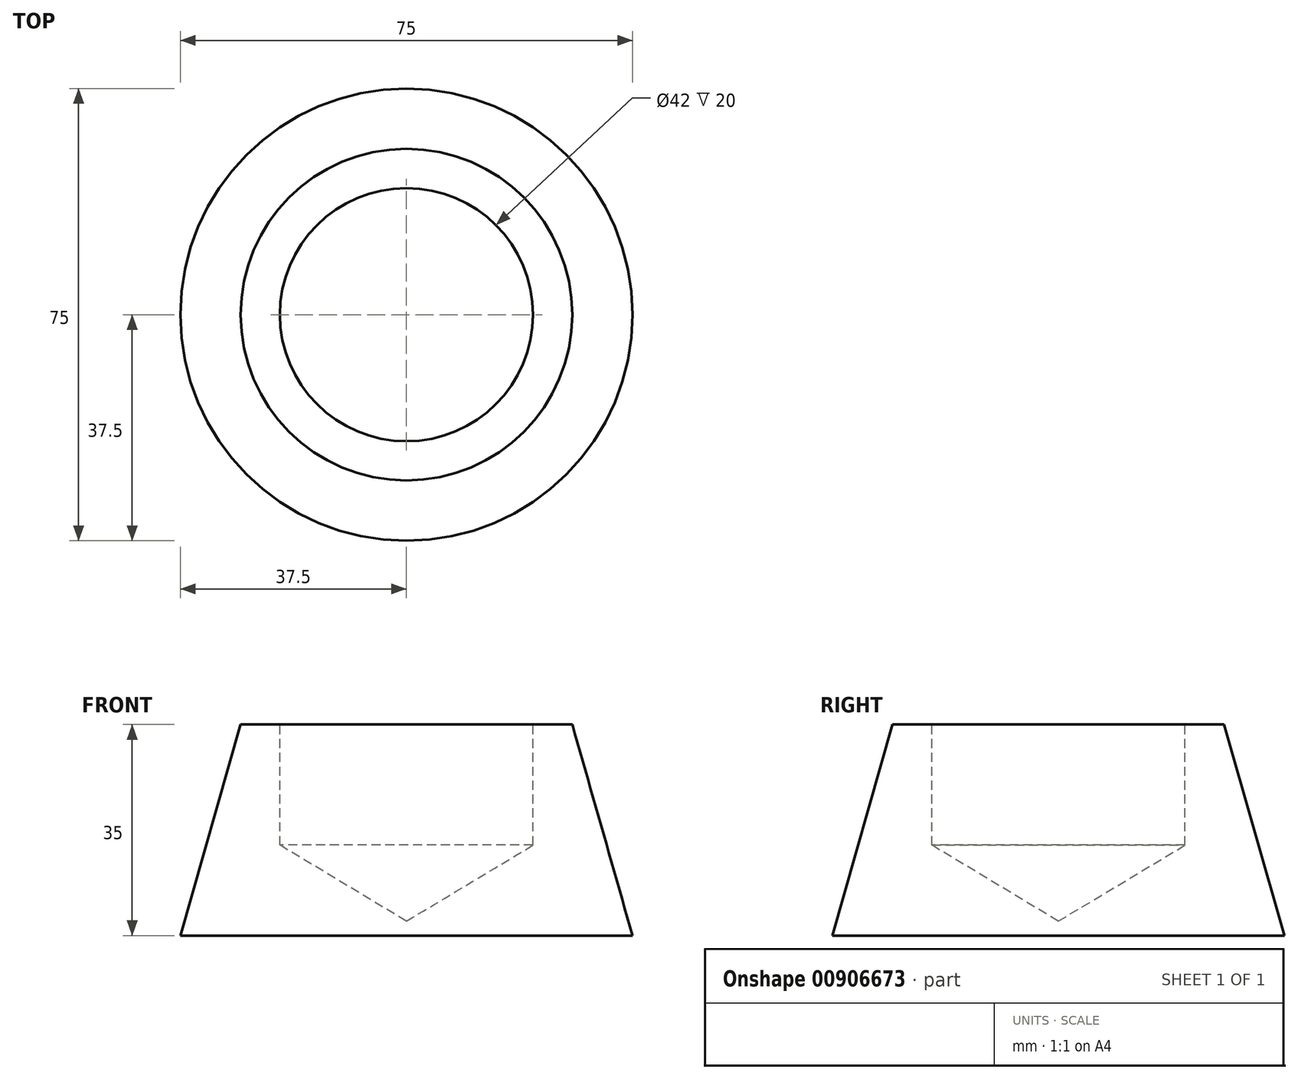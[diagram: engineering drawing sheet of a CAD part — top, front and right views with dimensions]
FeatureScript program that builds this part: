
annotation { "Feature Type Name" : "Feature", "Feature Type Description" : "" }
export const myFeature = defineFeature(function(context is Context, id is Id, definition is map)
    precondition{}
    {
        {
            var Q0;
            Q0=qCreatedBy(makeId("Top.planeOp"),FACE);
            var sketch = newSketch(context, id + "F0", { "sketchPlane" : qUnion([Q0])});
            skCircle(sketch, "E0", {"center": v(0, 0) * mm, "radius": 37.5 * mm});
            skSolve(sketch);
        }
        {
            var Q0;
            Q0=qCreatedBy(makeId("Top.planeOp"),FACE);
            cPlane(context, id + "F1", {"entities" : qUnion([Q0]), "cplaneType" : CPlaneType.OFFSET, "offset" : 35 * mm, "width" : 150 * mm, "height" : 150 * mm});
        }
        {
            var Q0;
            Q0=qCreatedBy(id+"F1.planeOp",FACE);
            var sketch = newSketch(context, id + "F2", { "sketchPlane" : qUnion([Q0])});
            skCircle(sketch, "E1", {"center": v(0, 0) * mm, "radius": 27.5 * mm});
            skSolve(sketch);
        }
        {
            var Q0;
            Q0=makeQuery(id+"F0.imprint","IMPRINT",FACE,{"disambiguationData":[TD([[makeQuery(id+"F0.imprint","IMPRINT",EDGE,{"derivedFrom":sQuery(id+"F0.wireOp",EDGE,"E0")}),1.0]])]});
            var Q1;
            Q1=makeQuery(id+"F2.imprint","IMPRINT",FACE,{"disambiguationData":[TD([[makeQuery(id+"F2.imprint","IMPRINT",EDGE,{"derivedFrom":sQuery(id+"F2.wireOp",EDGE,"E1")}),1.0]])]});
            loft(context, id + "F3", {"sheetProfilesArray" : [{ "sheetProfileEntities" : qUnion([Q0]) }, { "sheetProfileEntities" : qUnion([Q1]) }]});
        }
        {
            var Q0;
            Q0=sQuery(id+"F2.wireOp",VERTEX,"E1.center");
            var Q1;
            Q1=makeQuery(id+"F3.opLoft","SWEPT_BODY",BODY,{"disambiguationData":[OSD([makeQuery(id+"F0.imprint","IMPRINT",FACE,{"disambiguationData":[TD([[makeQuery(id+"F0.imprint","IMPRINT",EDGE,{"derivedFrom":sQuery(id+"F0.wireOp",EDGE,"E0")}),1.0]])]}),makeQuery(id+"F2.imprint","IMPRINT",FACE,{"disambiguationData":[TD([[makeQuery(id+"F2.imprint","IMPRINT",EDGE,{"derivedFrom":sQuery(id+"F2.wireOp",EDGE,"E1")}),1.0]])]})])]});
            hole(context, id + "F4", {"style" : HoleStyle.SIMPLE, "endStyle" : HoleEndStyle.BLIND, "holeDiameter" : 42 * mm, "majorDiameter" : 31.75 * mm, "holeDepth" : 20 * mm, "isTappedThrough" : true, "tappedDepth" : 12 * mm, "tapClearance" : 0, "locations" : qUnion([Q0]), "scope" : qUnion([Q1])});
        }
    });
